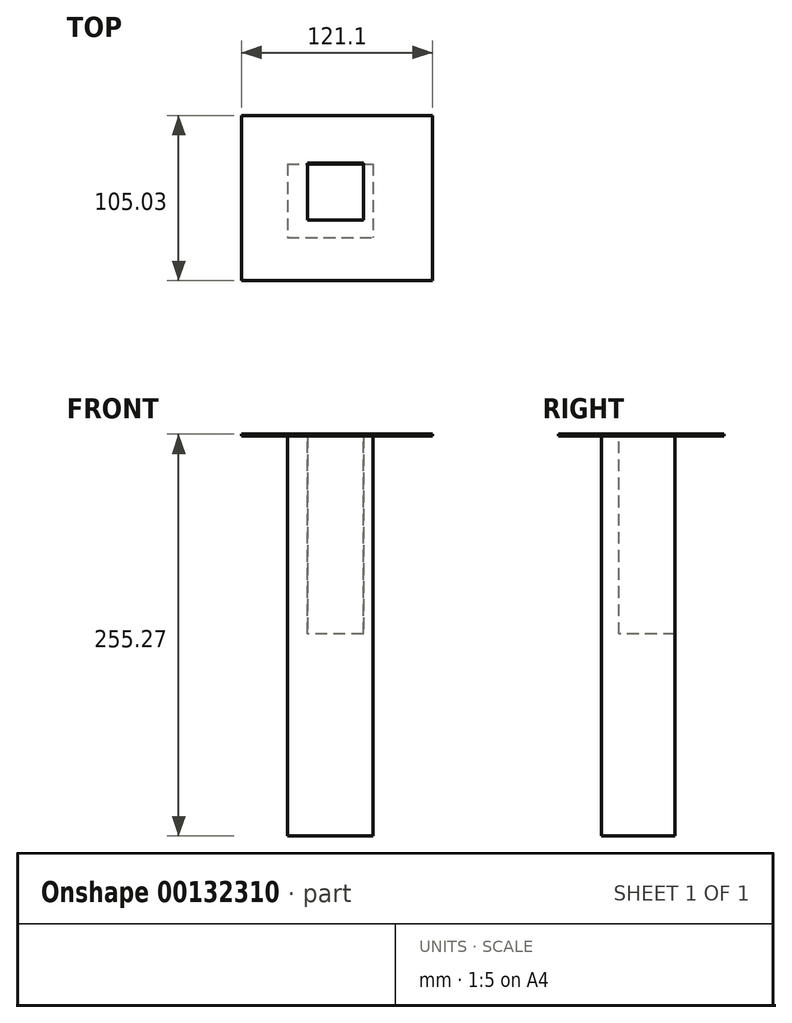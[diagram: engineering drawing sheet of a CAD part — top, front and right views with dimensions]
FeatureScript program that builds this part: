
annotation { "Feature Type Name" : "Feature", "Feature Type Description" : "" }
export const myFeature = defineFeature(function(context is Context, id is Id, definition is map)
    precondition{}
    {
        {
            var Q0;
            Q0=qCreatedBy(makeId("Top.planeOp"),FACE);
            var sketch = newSketch(context, id + "F0", { "sketchPlane" : qUnion([Q0])});
            skLineSegment(sketch, "E0.bottom", {"start": v(-47.26, 42.01) * mm, "end": v(48.5, 42.01) * mm});
            skLineSegment(sketch, "E0.top", {"start": v(-47.26, -37.38) * mm, "end": v(48.5, -37.38) * mm});
            skLineSegment(sketch, "E0.left", {"start": v(-47.26, 42.01) * mm, "end": v(-47.26, -37.38) * mm});
            skLineSegment(sketch, "E0.right", {"start": v(48.5, 42.01) * mm, "end": v(48.5, -37.38) * mm});
            skLineSegment(sketch, "E1.bottom", {"start": v(-28.73, 22.86) * mm, "end": v(25.64, 22.86) * mm});
            skLineSegment(sketch, "E1.top", {"start": v(-28.73, -23.79) * mm, "end": v(25.64, -23.79) * mm});
            skLineSegment(sketch, "E1.left", {"start": v(-28.73, 22.86) * mm, "end": v(-28.73, -23.79) * mm});
            skLineSegment(sketch, "E1.right", {"start": v(25.64, 22.86) * mm, "end": v(25.64, -23.79) * mm});
            skSolve(sketch);
        }
        {
            var Q0;
            Q0=qCreatedBy(makeId("Top.planeOp"),FACE);
            var sketch = newSketch(context, id + "F1", { "sketchPlane" : qUnion([Q0])});
            skLineSegment(sketch, "E2.bottom", {"start": v(-57.77, 53.75) * mm, "end": v(63.33, 53.75) * mm});
            skLineSegment(sketch, "E2.top", {"start": v(-57.77, -51.28) * mm, "end": v(63.33, -51.28) * mm});
            skLineSegment(sketch, "E2.left", {"start": v(-57.77, 53.75) * mm, "end": v(-57.77, -51.28) * mm});
            skLineSegment(sketch, "E2.right", {"start": v(63.33, 53.75) * mm, "end": v(63.33, -51.28) * mm});
            skSolve(sketch);
        }
        {
            var Q0;
            Q0=makeQuery(id+"F0.imprint","IMPRINT",FACE,{"disambiguationData":[TD([[makeQuery(id+"F0.imprint","IMPRINT",EDGE,{"derivedFrom":sQuery(id+"F0.wireOp",EDGE,"E1.bottom")}),-1.0]])]});
            extrude(context, id + "F2", {"entities" : qUnion([Q0]), "oppositeDirection" : true, "depth" : 254 * mm});
        }
        {
            var Q0;
            Q0=makeQuery(id+"F1.imprint","IMPRINT",FACE,{"disambiguationData":[TD([[makeQuery(id+"F1.imprint","IMPRINT",EDGE,{"derivedFrom":sQuery(id+"F1.wireOp",EDGE,"E2.bottom")}),-1.0]])]});
            extrude(context, id + "F3", {"entities" : qUnion([Q0]), "operationType" : NewBodyOperationType.ADD, "depth" : 1.27 * mm});
        }
        {
            var Q0;
            Q0=makeQuery(id+"F3.opExtrude","CAP_FACE",FACE,{"disambiguationData":[OSD([sQuery(id+"F1.wireOp",EDGE,"E2.bottom"),sQuery(id+"F1.wireOp",EDGE,"E2.top"),sQuery(id+"F1.wireOp",EDGE,"E2.left"),sQuery(id+"F1.wireOp",EDGE,"E2.right")])],"isStart":false});
            var sketch = newSketch(context, id + "F4", { "sketchPlane" : qUnion([Q0])});
            skLineSegment(sketch, "E3.bottom", {"start": v(-16.06, 23.48) * mm, "end": v(19.46, 23.48) * mm});
            skLineSegment(sketch, "E3.top", {"start": v(-16.06, -12.67) * mm, "end": v(19.46, -12.67) * mm});
            skLineSegment(sketch, "E3.left", {"start": v(-16.06, 23.48) * mm, "end": v(-16.06, -12.67) * mm});
            skLineSegment(sketch, "E3.right", {"start": v(19.46, 23.48) * mm, "end": v(19.46, -12.67) * mm});
            skSolve(sketch);
        }
        {
            var Q0;
            Q0=makeQuery(id+"F4.imprint","IMPRINT",FACE,{"disambiguationData":[TD([[makeQuery(id+"F4.imprint","IMPRINT",EDGE,{"derivedFrom":sQuery(id+"F4.wireOp",EDGE,"E3.bottom")}),-1.0]])]});
            extrude(context, id + "F5", {"entities" : qUnion([Q0]), "operationType" : NewBodyOperationType.REMOVE, "oppositeDirection" : true, "depth" : 127 * mm});
        }
    });
